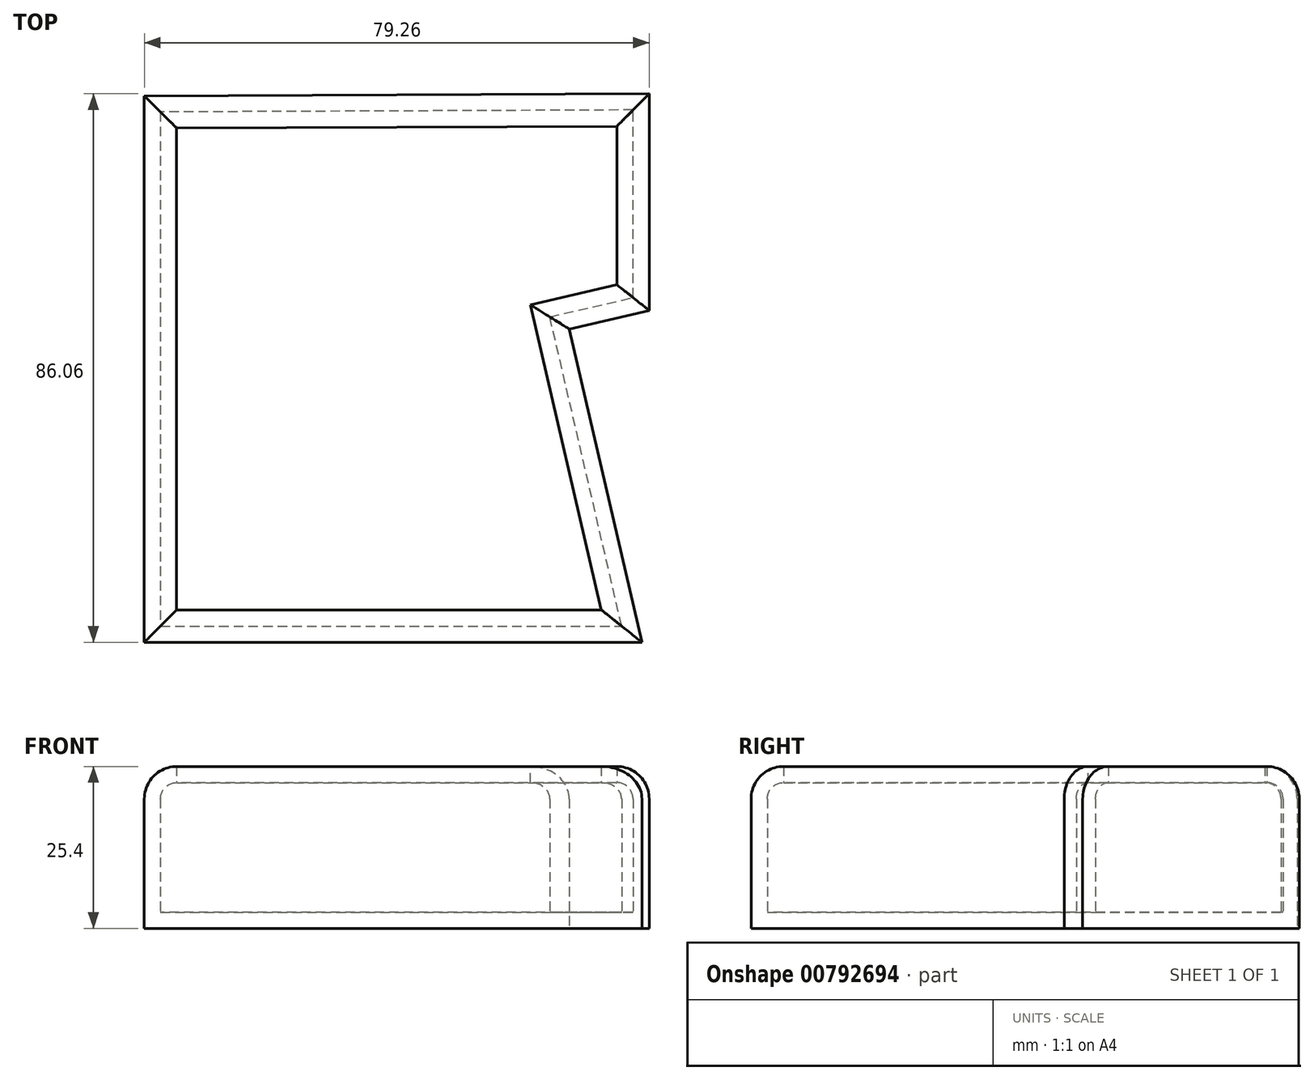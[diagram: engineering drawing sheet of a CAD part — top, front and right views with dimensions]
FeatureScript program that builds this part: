
annotation { "Feature Type Name" : "Feature", "Feature Type Description" : "" }
export const myFeature = defineFeature(function(context is Context, id is Id, definition is map)
    precondition{}
    {
        {
            var Q0;
            Q0=qCreatedBy(makeId("Top.planeOp"),FACE);
            var sketch = newSketch(context, id + "F0", { "sketchPlane" : qUnion([Q0])});
            skLineSegment(sketch, "E0", {"start": v(-35.08, 53.81) * mm, "end": v(-35.08, -31.91) * mm});
            skLineSegment(sketch, "E1", {"start": v(-35.08, -31.91) * mm, "end": v(43.05, -31.91) * mm});
            skLineSegment(sketch, "E2", {"start": v(43.05, -31.91) * mm, "end": v(31.64, 17.23) * mm});
            skLineSegment(sketch, "E3", {"start": v(31.64, 17.23) * mm, "end": v(44.18, 20.15) * mm});
            skLineSegment(sketch, "E4", {"start": v(44.18, 20.15) * mm, "end": v(44.18, 46.18) * mm});
            skLineSegment(sketch, "E5", {"start": v(44.18, 46.18) * mm, "end": v(44.18, 54.15) * mm});
            skLineSegment(sketch, "E6", {"start": v(44.18, 54.15) * mm, "end": v(-35.08, 53.81) * mm});
            skSolve(sketch);
        }
        {
            var Q0;
            Q0=makeQuery(id+"F0.imprint","IMPRINT",FACE,{"disambiguationData":[TD([[makeQuery(id+"F0.imprint","IMPRINT",EDGE,{"derivedFrom":sQuery(id+"F0.wireOp",EDGE,"E0")}),1.0]])]});
            extrude(context, id + "F1", {"entities" : qUnion([Q0]), "depth" : 25.4 * mm, "offsetDistance" : 25.4 * mm});
        }
        {
            var Q0;
            Q0=makeQuery(id+"F1.opExtrude","CAP_FACE",FACE,{"disambiguationData":[OSD([sQuery(id+"F0.wireOp",EDGE,"E0"),sQuery(id+"F0.wireOp",EDGE,"E1"),sQuery(id+"F0.wireOp",EDGE,"E2"),sQuery(id+"F0.wireOp",EDGE,"E3"),sQuery(id+"F0.wireOp",EDGE,"E4"),sQuery(id+"F0.wireOp",EDGE,"E5"),sQuery(id+"F0.wireOp",EDGE,"E6")])],"isStart":false});
            fillet(context, id + "F2", {"entities" : qUnion([Q0]), "radius" : 5.08 * mm, "tangentPropagation" : true, "allowEdgeOverflow" : false});
        }
        {
            var Q0;
            Q0=makeQuery(id+"F1.opExtrude","CAP_FACE",FACE,{"disambiguationData":[OSD([sQuery(id+"F0.wireOp",EDGE,"E0"),sQuery(id+"F0.wireOp",EDGE,"E1"),sQuery(id+"F0.wireOp",EDGE,"E2"),sQuery(id+"F0.wireOp",EDGE,"E3"),sQuery(id+"F0.wireOp",EDGE,"E4"),sQuery(id+"F0.wireOp",EDGE,"E5"),sQuery(id+"F0.wireOp",EDGE,"E6")])],"isStart":false});
            shell(context, id + "F3", {"entities" : qUnion([Q0]), "thickness" : 2.54 * mm});
        }
    });
